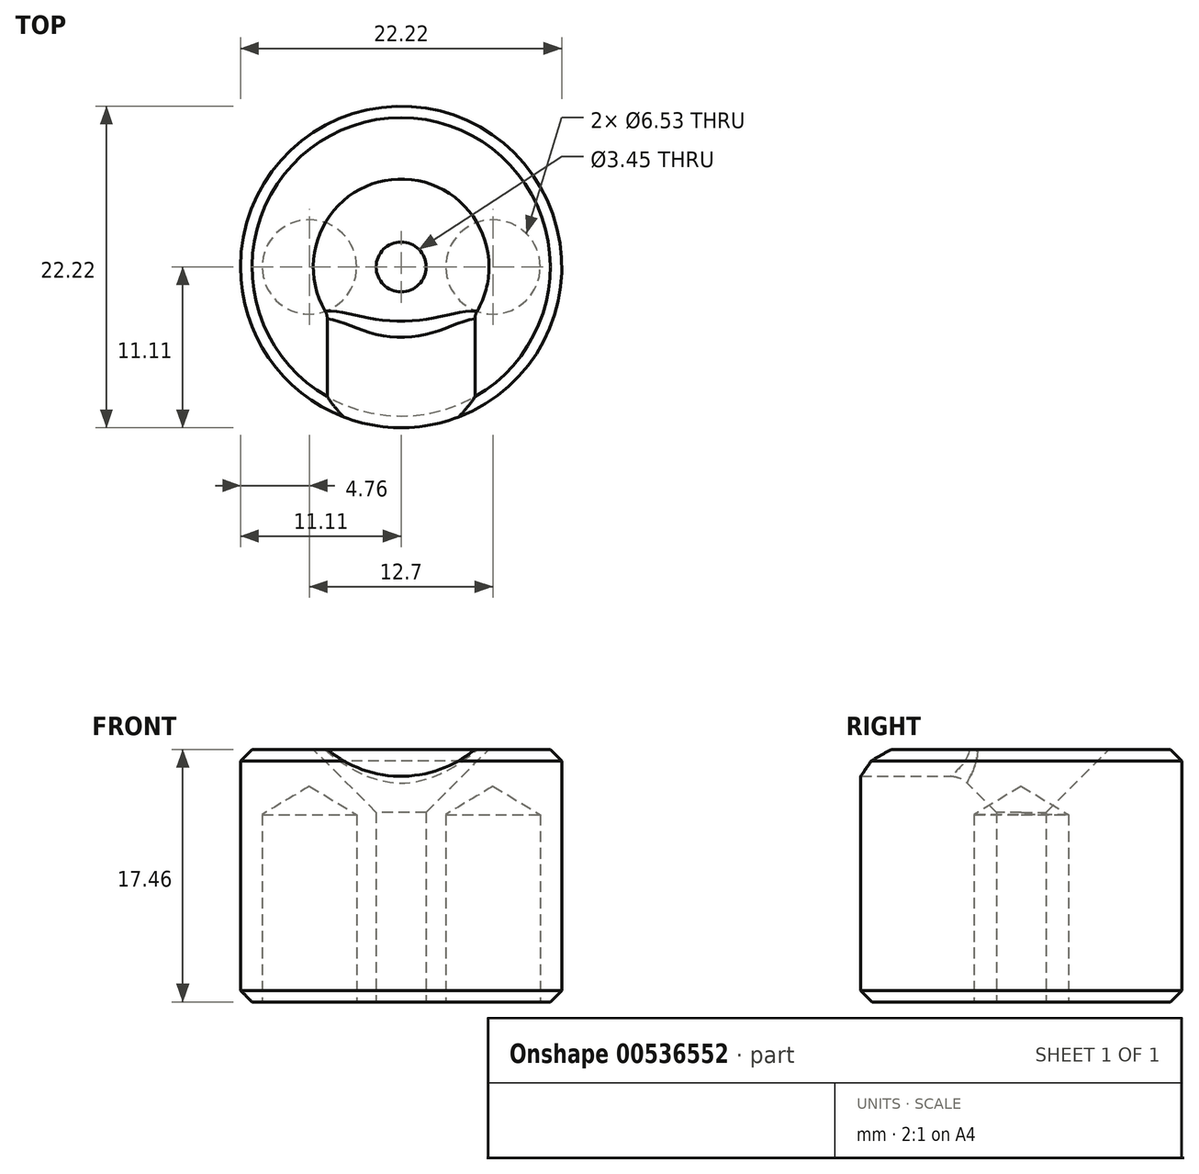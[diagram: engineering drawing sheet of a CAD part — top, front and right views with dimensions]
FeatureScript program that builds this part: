
annotation { "Feature Type Name" : "Feature", "Feature Type Description" : "" }
export const myFeature = defineFeature(function(context is Context, id is Id, definition is map)
    precondition{}
    {
        {
            var Q0;
            Q0=qCreatedBy(makeId("Front.planeOp"),FACE);
            var sketch = newSketch(context, id + "F0", { "sketchPlane" : qUnion([Q0])});
            skLineSegment(sketch, "E0", {"start": v(0, 0) * mm, "end": v(-11.11, 0) * mm});
            skLineSegment(sketch, "E1", {"start": v(-7.67, 0) * mm, "end": v(-7.67, 19.05) * mm, "construction": true});
            skLineSegment(sketch, "E2", {"start": v(-7.67, 19.05) * mm, "end": v(0, 11.38) * mm, "construction": true});
            skLineSegment(sketch, "E3", {"start": v(0, 0) * mm, "end": v(0, 11.38) * mm});
            skCircle(sketch, "E4", {"center": v(0, 20.37) * mm, "radius": 6.35 * mm, "construction": true});
            skPoint(sketch, "E5", {"position": v(-4.5, 15.88) * mm});
            skLineSegment(sketch, "E6", {"start": v(-11.11, 17.46) * mm, "end": v(-6.08, 17.46) * mm});
            skLineSegment(sketch, "E7", {"start": v(-11.11, 0) * mm, "end": v(-11.11, 17.46) * mm});
            skLineSegment(sketch, "E8", {"start": v(-6.08, 17.46) * mm, "end": v(0, 11.38) * mm});
            skSolve(sketch);
        }
        {
            var Q0;
            Q0=makeQuery(id+"F0.imprint","IMPRINT",FACE,{"disambiguationData":[TD([[makeQuery(id+"F0.imprint","IMPRINT",EDGE,{"derivedFrom":sQuery(id+"F0.wireOp",EDGE,"E0")}),-1.0]])]});
            var Q1;
            Q1=sQuery(id+"F0.wireOp",EDGE,"9J9QawgG-At0g-vajj-XDBG-oqsChZEEckl1");
            var Q2;
            Q2=sQuery(id+"F0.wireOp",EDGE,"n1MmJU6g-dmth-fbbE-oKrD-CuxaOYQL0cR0");
            var Q3;
            Q3=sQuery(id+"F0.wireOp",EDGE,"KnCWZ9pG-3dk9-LInL-IE6G-YEWYwB7tTK2N");
            var Q4;
            Q4=sQuery(id+"F0.wireOp",EDGE,"E3");
            var Q5;
            Q5=sQuery(id+"F0.wireOp",EDGE,"E8");
            var Q6;
            Q6=sQuery(id+"F0.wireOp",EDGE,"E6");
            var Q7;
            Q7=sQuery(id+"F0.wireOp",EDGE,"E7");
            var Q8;
            Q8=sQuery(id+"F0.wireOp",EDGE,"E0");
            var Q9;
            Q9=sQuery(id+"F0.wireOp",EDGE,"E3");
            revolve(context, id + "F1", {"entities" : qUnion([Q0]), "surfaceEntities" : qUnion([Q1, Q2, Q3, Q4, Q5, Q6, Q7, Q8]), "axis" : qUnion([Q9]), "revolveType" : RevolveType.FULL});
        }
        {
            var Q0;
            Q0=makeQuery(id+"F1.opRevolve","SWEPT_EDGE",EDGE,{"disambiguationData":[OSD([sQuery(id+"F0.wireOp",EDGE,"E0"),sQuery(id+"F0.wireOp",EDGE,"E7")])]});
            var Q1;
            Q1=makeQuery(id+"F1.opRevolve","SWEPT_EDGE",EDGE,{"disambiguationData":[OSD([sQuery(id+"F0.wireOp",EDGE,"E6"),sQuery(id+"F0.wireOp",EDGE,"E7")])]});
            chamfer(context, id + "F2", {"entities" : qUnion([Q0, Q1]), "width" : 0.8 * mm, "tangentPropagation" : true});
        }
        {
            var Q0;
            Q0=qCreatedBy(makeId("Front.planeOp"),FACE);
            var sketch = newSketch(context, id + "F3", { "sketchPlane" : qUnion([Q0])});
            skCircle(sketch, "E9", {"center": v(0, 20.37) * mm, "radius": 6.35 * mm, "construction": true});
            skCircle(sketch, "E10", {"center": v(0, 23.54) * mm, "radius": 7.94 * mm});
            skLineSegment(sketch, "E11", {"start": v(0, 23.54) * mm, "end": v(0, 20.37) * mm, "construction": true});
            skPoint(sketch, "E12", {"position": v(0, 15.6) * mm});
            skSolve(sketch);
        }
        {
            var Q0;
            Q0 = qSketchRegion(id + "F3", true);
            extrude(context, id + "F4", {"entities" : qUnion([Q0]), "operationType" : NewBodyOperationType.REMOVE, "depth" : 25.4 * mm, "offsetDistance" : 25.4 * mm});
        }
        {
            var Q0;
            Q0=makeQuery(id+"F4.boolean.opBoolean","INTERSECT",EDGE,{"derivedFrom":[makeQuery(id+"F1.opRevolve","SWEPT_FACE",FACE,{"disambiguationData":[OSD([sQuery(id+"F0.wireOp",EDGE,"E8")])]}),makeQuery(id+"F4.opExtrude","SWEPT_FACE",FACE,{"disambiguationData":[OSD([sQuery(id+"F3.wireOp",EDGE,"E10")])]})]});
            fillet(context, id + "F5", {"entities" : qUnion([Q0]), "radius" : 1.59 * mm, "tangentPropagation" : true, "allowEdgeOverflow" : false});
        }
        {
            var Q0;
            Q0=makeQuery(id+"F1.opRevolve","SWEPT_FACE",FACE,{"disambiguationData":[OSD([sQuery(id+"F0.wireOp",EDGE,"E0")])]});
            var sketch = newSketch(context, id + "F6", { "sketchPlane" : qUnion([Q0])});
            skPoint(sketch, "E13", {"position": v(0, 0) * mm});
            skLineSegment(sketch, "E14", {"start": v(0, 0) * mm, "end": v(6.35, 0) * mm, "construction": true});
            skLineSegment(sketch, "E15", {"start": v(0, 0) * mm, "end": v(-6.35, 0) * mm, "construction": true});
            skCircle(sketch, "E16", {"center": v(6.35, 0) * mm, "radius": 3.31 * mm, "construction": true});
            skCircle(sketch, "E17", {"center": v(-6.35, 0) * mm, "radius": 3.31 * mm, "construction": true});
            skSolve(sketch);
        }
        {
            var Q0;
            Q0=sQuery(id+"F6.wireOp",VERTEX,"E13");
            var Q1;
            Q1=makeQuery(id+"F1.opRevolve","SWEPT_BODY",BODY,{"disambiguationData":[OSD([sQuery(id+"F0.wireOp",EDGE,"E0"),sQuery(id+"F0.wireOp",EDGE,"E3"),sQuery(id+"F0.wireOp",EDGE,"E6"),sQuery(id+"F0.wireOp",EDGE,"E7"),sQuery(id+"F0.wireOp",EDGE,"E8")])]});
            hole(context, id + "F7", {"style" : HoleStyle.SIMPLE, "endStyle" : HoleEndStyle.THROUGH, "standardTappedOrClearance" : lookupTablePath({ "standard" : "ANSI", "engagement" : "75%", "pitch" : "36 tpi", "size" : "#8", "type" : "Tapped" }), "standardBlindInLast" : lookupTablePath({ "standard" : "ANSI", "engagement" : "75%", "pitch" : "36 tpi", "size" : "#8", "type" : "Tapped" }), "holeDiameter" : 3.45 * mm, "showTappedDepth" : true, "tappedDepth" : 25.4 * mm, "tapClearance" : 3, "startFromSketch" : true, "locations" : qUnion([Q0]), "scope" : qUnion([Q1]), "majorDiameter" : 4.17 * mm});
        }
        {
            var Q0;
            Q0=sQuery(id+"F6.wireOp",VERTEX,"E14.end");
            var Q1;
            Q1=sQuery(id+"F6.wireOp",VERTEX,"E17.center");
            var Q2;
            Q2=makeQuery(id+"F1.opRevolve","SWEPT_BODY",BODY,{"disambiguationData":[OSD([sQuery(id+"F0.wireOp",EDGE,"E0"),sQuery(id+"F0.wireOp",EDGE,"E3"),sQuery(id+"F0.wireOp",EDGE,"E6"),sQuery(id+"F0.wireOp",EDGE,"E7"),sQuery(id+"F0.wireOp",EDGE,"E8")])]});
            hole(context, id + "F8", {"style" : HoleStyle.SIMPLE, "endStyle" : HoleEndStyle.BLIND, "standardTappedOrClearance" : lookupTablePath({ "standard" : "ANSI", "size" : "F (0.26)", "type" : "Drilled" }), "standardBlindInLast" : lookupTablePath({ "standard" : "ANSI", "size" : "F", "type" : "Drilled" }), "holeDiameter" : 6.53 * mm, "holeDepth" : 12.95 * mm, "tappedDepth" : 25.4 * mm, "tapClearance" : 3, "startFromSketch" : true, "locations" : qUnion([Q0, Q1]), "scope" : qUnion([Q2])});
        }
    });
